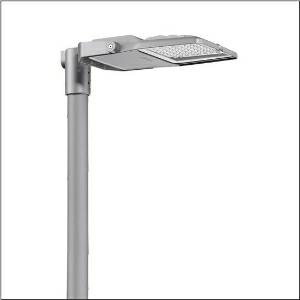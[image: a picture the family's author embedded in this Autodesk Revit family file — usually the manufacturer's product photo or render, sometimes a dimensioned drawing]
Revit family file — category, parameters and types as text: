
# Revit family: floodlight_fl_21_iq_mini___pl61_5xa7771c4c3a_1011
name_source: partatom
category: Lighting Fixtures
units: mm (PartAtom-declared; Revit-internal decimal feet)

## family parameters
Cut with Voids When Loaded = No
Host = Face
Light Source = No
Part Type = Normal
Room Calculation Point = No
Round Connector Dimension = Use Diameter
Shared = No

## types (1)
- --- (1 x LED, 12490 lm, 87.2 W, 4000K)
    Apparent Load = 87 VA
    CIE Flux Codes = 33 65 98 100 100
    Color Rendering = 70
    Color Temperature = 4000K
    Default Elevation = 1800 mm
    Description = Floodlight FL 21 iQ mini, floodlight, primary light control with lens, of PMMA, primary optical cover: protective disc, of toughened safety glass, transparent, light distribution: PL61, light emission: direct distribution, installation type: surface-mounted, LED, High Power LED, rated luminous flux: 12.490lm, luminous efficacy: 143lm/W, light colour: 740, colour temperature: 4000K, control gear: iQ Comfort/DALI, control: Auto-Match, Temp-Guard, Lumen-Switch, Night-Set, Smart-Wire, Light-Fading, Desk-Remote (wireless, voltage-free reading and setting of iQ features in the workshop via application-optimized NFC function/RFID function), optimised constant luminous flux control (CLO 2.0), with terminal, 6-pole, mains connection: 220..240V, AC, 50/60Hz, start of lifetime: 87W, end of service life: 92W, reduction: 40W, luminaire housing, of diecast aluminium, powder-coated, Siteco® metallic grey (DB 702S), corrosivity category C5 mid according to DIN EN ISO 12944, suitable for swimming pools, chlorine-resistant, sealing non-destructively replaceable, please order mast flange separately, mast bracket, of steel, galvanised, powder-coated, Siteco® metallic grey (DB 702S), protection rating (complete): IP66, insulation class (complete): insulation class II (safety insulation), certification: CE, ENEC, VDE, protection symbol: D, impact resistance: IK08, permissible operating ambient temperature: -40..+40°C, permissible operating ambient temperature for outdoor applications: -40..+50°C, standard: DIN EN 12944, LABS conformity tested according to VDMA 24364:2018-05, packaging unit: 1 piece

Light Distribution: PL61
    Height = 70 mm
    Lamp = 1 x LED
    Lamp Light Flux = 12490 lm
    Lamp Power = 87.2 W
    Lamp count = 1
    Length = 485 mm
    Luminous efficacy = 143 lm/W
    Manufacturer = Siteco
    ModVariant = No
    Model = 5XA7771C4C3A
    Number of Poles = 1
    OnlyDefault = Yes
    Power Factor = 1
    Product Name = Floodlight FL 21 iQ mini | PL61
    Product group = floodlight | pylon annexe
    ProductGroupID = 6201
    Protection Class = Protection class II
    Protection Degree = IP 66
    RLX_Detail_Level = 1
    RLX_Emergency_Light_Flux = 0 lm
    RLX_Emergency_Type = 0
    RLX_Emergency_Type_DB = No
    RlxData = <blob elided: 101497 chars, md5=d835d553>
    Socket = socket
    Standby Power = 0 W
    System Light Flux = 12490 lm
    System Power = 87 W
    Type Comments = factory setting: luminous flux: 100 % | dim-lin: 254 | 456 mA
    Type Image = l_1007125.jpg
    URL = http://relux.com
    VarID = @adj_194661
    Voltage = 0 V
    Weight = 0.00 kg
    Width = 337 mm

## geometry (parser evidence)
native form markers: Blend x4, Sweep x11
no freeform markers — native parametric forms only
